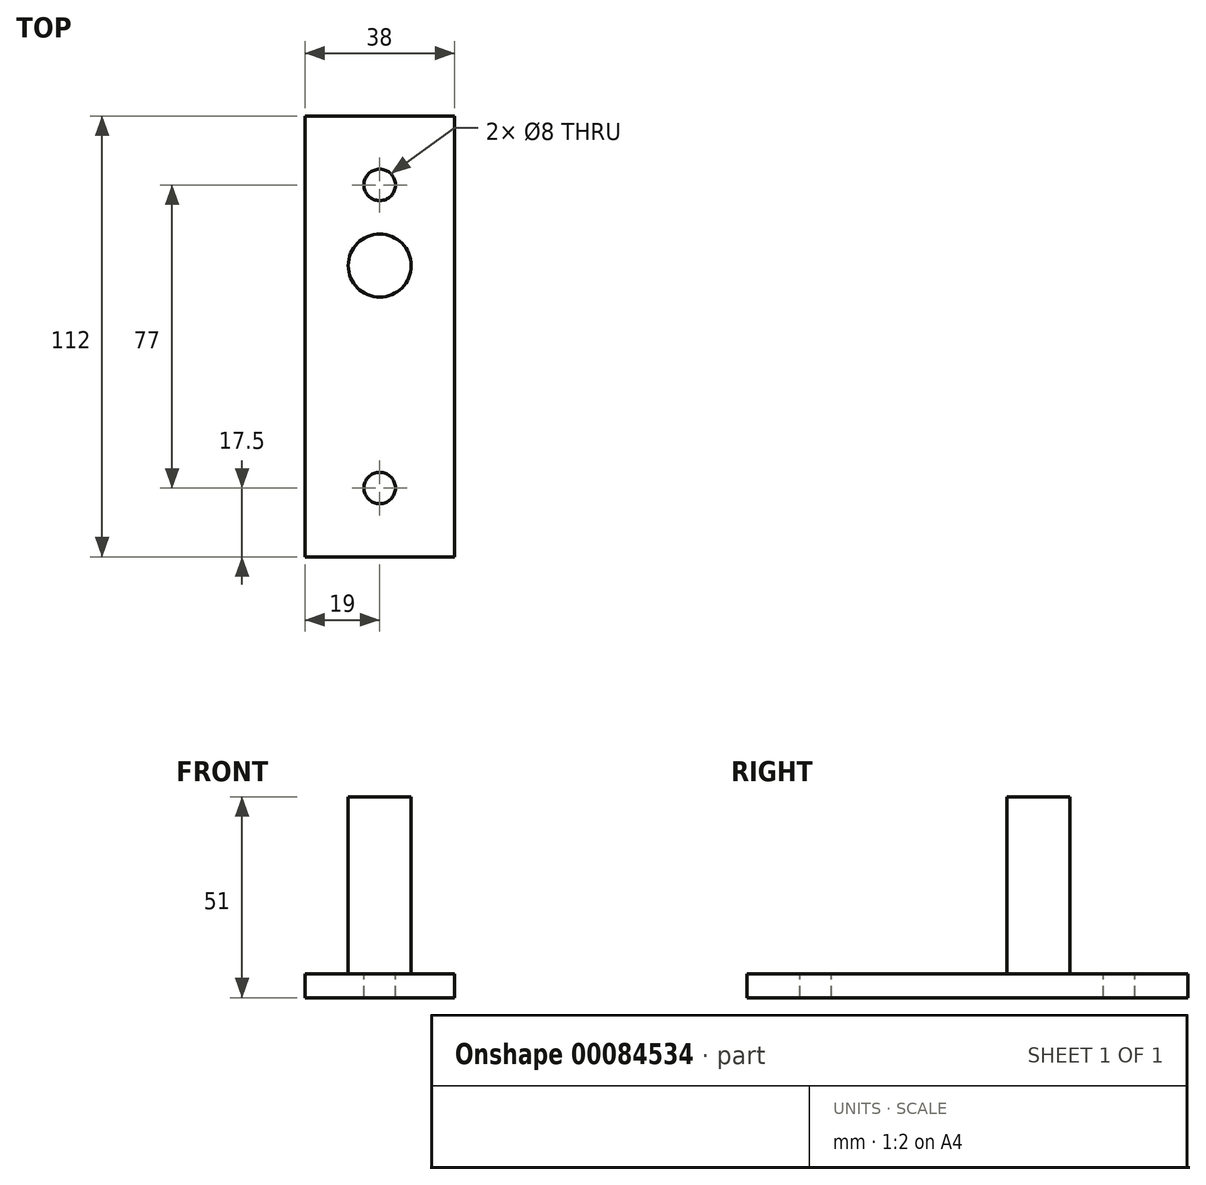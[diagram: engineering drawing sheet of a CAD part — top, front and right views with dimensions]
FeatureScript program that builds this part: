
annotation { "Feature Type Name" : "Feature", "Feature Type Description" : "" }
export const myFeature = defineFeature(function(context is Context, id is Id, definition is map)
    precondition{}
    {
        {
            var Q0;
            Q0=qCreatedBy(makeId("Top.planeOp"),FACE);
            var sketch = newSketch(context, id + "F0", { "sketchPlane" : qUnion([Q0])});
            skLineSegment(sketch, "E0", {"start": v(-19, 0) * mm, "end": v(-19, 56) * mm});
            skLineSegment(sketch, "E1", {"start": v(0, 56) * mm, "end": v(-19, 56) * mm});
            skLineSegment(sketch, "E2.MirrorCS", {"start": v(0, -56) * mm, "end": v(-19, -56) * mm});
            skLineSegment(sketch, "E3.MirrorCS", {"start": v(-19, 0) * mm, "end": v(-19, -56) * mm});
            skLineSegment(sketch, "E4.MirrorCS", {"start": v(0, 56) * mm, "end": v(19, 56) * mm});
            skLineSegment(sketch, "E5.MirrorCS", {"start": v(19, 0) * mm, "end": v(19, 56) * mm});
            skLineSegment(sketch, "E6.MirrorCS", {"start": v(19, 0) * mm, "end": v(19, -56) * mm});
            skLineSegment(sketch, "E7.MirrorCS", {"start": v(0, -56) * mm, "end": v(19, -56) * mm});
            skSolve(sketch);
        }
        {
            var Q0;
            Q0 = qSketchRegion(id + "F0", true);
            var Q1;
            Q1 = qSketchRegion(id + "F2", true);
            extrude(context, id + "F1", {"entities" : qUnion([Q0, Q1]), "depth" : 6 * mm});
        }
        {
            var Q0;
            Q0=makeQuery(id+"F1.opExtrude","CAP_FACE",FACE,{"disambiguationData":[OSD([sQuery(id+"F0.wireOp",EDGE,"E0"),sQuery(id+"F0.wireOp",EDGE,"E1"),sQuery(id+"F0.wireOp",EDGE,"E2.MirrorCS"),sQuery(id+"F0.wireOp",EDGE,"E3.MirrorCS"),sQuery(id+"F0.wireOp",EDGE,"E4.MirrorCS"),sQuery(id+"F0.wireOp",EDGE,"E5.MirrorCS"),sQuery(id+"F0.wireOp",EDGE,"E6.MirrorCS"),sQuery(id+"F0.wireOp",EDGE,"E7.MirrorCS")])],"isStart":false});
            var sketch = newSketch(context, id + "F2", { "sketchPlane" : qUnion([Q0])});
            skCircle(sketch, "E8", {"center": v(0, 38.5) * mm, "radius": 4 * mm});
            skCircle(sketch, "E9.MirrorC", {"center": v(0, -38.5) * mm, "radius": 4 * mm});
            skSolve(sketch);
        }
        {
            var Q0;
            Q0 = qSketchRegion(id + "F2", true);
            extrude(context, id + "F3", {"entities" : qUnion([Q0]), "operationType" : NewBodyOperationType.REMOVE, "endBound" : BoundingType.THROUGH_ALL, "oppositeDirection" : true, "depth" : 25.4 * mm});
        }
        {
            var Q0;
            Q0=makeQuery(id+"F1.opExtrude","CAP_FACE",FACE,{"disambiguationData":[OSD([sQuery(id+"F0.wireOp",EDGE,"E0"),sQuery(id+"F0.wireOp",EDGE,"E1"),sQuery(id+"F0.wireOp",EDGE,"E2.MirrorCS"),sQuery(id+"F0.wireOp",EDGE,"E3.MirrorCS"),sQuery(id+"F0.wireOp",EDGE,"E4.MirrorCS"),sQuery(id+"F0.wireOp",EDGE,"E5.MirrorCS"),sQuery(id+"F0.wireOp",EDGE,"E6.MirrorCS"),sQuery(id+"F0.wireOp",EDGE,"E7.MirrorCS")])],"isStart":false});
            var sketch = newSketch(context, id + "F4", { "sketchPlane" : qUnion([Q0])});
            skCircle(sketch, "E10", {"center": v(0, 18) * mm, "radius": 8 * mm});
            skSolve(sketch);
        }
        {
            var Q0;
            Q0 = qSketchRegion(id + "F4", true);
            extrude(context, id + "F5", {"entities" : qUnion([Q0]), "operationType" : NewBodyOperationType.ADD, "depth" : 45 * mm});
        }
    });
